FCSTD DOCUMENT  (FreeCAD 0.17R11939 (Git))
Label: front_head_tube_position
License: All rights reserved
LicenseURL: http://en.wikipedia.org/wiki/All_rights_reserved
objects: Sketcher::SketchObject×1
note: 1 computed .brp shape members not serialized (recipe doc carries the construction recipe); baked Part::Feature solids carry a one-line shape summary decoded from their .brp

FEATURE [Sketcher::SketchObject] Sketch
  expr: Constraints[10] = 180 - 74
  sketch-geometry (17):
    g0: LineSegment StartX=25.7714 StartY=69.3917 StartZ=0 EndX=56.0915 EndY=-36.3471 EndZ=0
    g1: LineSegment StartX=20.5248 StartY=-46.5457 StartZ=0 EndX=-9.79528 EndY=59.1931 EndZ=0
    g2: LineSegment [constr] StartX=6.63271 StartY=1.9019 StartZ=0 EndX=42.1994 EndY=12.1005 EndZ=0
    g3: GeomPoint X=24.416 Y=7.00119 Z=0
    g4: LineSegment [constr] StartX=6.63271 StartY=1.9019 StartZ=0 EndX=0 EndY=0 EndZ=0
    g5: ArcOfCircle CenterX=0 CenterY=0 CenterZ=0 NormalX=0 NormalY=0 NormalZ=1 Radius=25.4 StartAngle=1.57494 EndAngle=5.26675
    g6: ArcOfCircle CenterX=0 CenterY=0 CenterZ=0 NormalX=0 NormalY=0 NormalZ=1 Radius=23.749 StartAngle=1.55526 EndAngle=5.28643
    g7: LineSegment [constr] StartX=-25.4 StartY=0 StartZ=0 EndX=-23.749 EndY=0 EndZ=0
    g8: LineSegment StartX=-9.79528 StartY=59.1931 StartZ=0 EndX=-8.20824 EndY=59.6482 EndZ=0
    g9: LineSegment StartX=-8.20824 StartY=59.6482 StartZ=0 EndX=22.1119 EndY=-46.0906 EndZ=0
    g10: LineSegment StartX=22.1119 StartY=-46.0906 StartZ=0 EndX=20.5248 EndY=-46.5457 EndZ=0
    g11: LineSegment StartX=25.7714 StartY=69.3917 StartZ=0 EndX=24.1844 EndY=68.9366 EndZ=0
    g12: LineSegment StartX=24.1844 StartY=68.9366 StartZ=0 EndX=54.5045 EndY=-36.8022 EndZ=0
    g13: LineSegment StartX=54.5045 StartY=-36.8022 StartZ=0 EndX=56.0915 EndY=-36.3471 EndZ=0
    g14: LineSegment [constr] StartX=-8.20824 StartY=59.6482 StartZ=0 EndX=24.1844 EndY=68.9366 EndZ=0
    g15: LineSegment [constr] StartX=22.1119 StartY=-46.0906 StartZ=0 EndX=54.5045 EndY=-36.8022 EndZ=0
    g16: LineSegment [constr] StartX=7.00122 StartY=-24.416 StartZ=0 EndX=13.6339 EndY=-22.5141 EndZ=0
  constraints (52):
    c: Parallel(g1,g0)
    c: Distance(g1) = 110
    c: PointOnObject(g2,g1)
    c: PointOnObject(g2,g0)
    c: Perpendicular(g0,g2)
    c: PointOnObject(g3,g2)
    c: Symmetric(g2,g2,g3)
    c: Coincident(g4,g2)
    c: Coincident(g4,g-1)
    c: Parallel(g4,g2)
    c: Angle(g1) = 1.85005
    c: Coincident(g5,g-1)
    c: PointOnObject(g5,g1)
    c: PointOnObject(g5,g1)
    c: Radius(g5) = 25.4
    c: Coincident(g6,g-1)
    c: PointOnObject(g6,g1)
    c: PointOnObject(g6,g1)
    c: Distance(g-1,g3) = 25.4
    c: PointOnObject(g7,g5)
    c: PointOnObject(g7,g6)
    c: Horizontal(g7)
    c: PointOnObject(g7,g-1)
    c: Distance(g7) = 1.651
    c: Coincident(g8,g1)
    c: Coincident(g9,g8)
    c: Coincident(g10,g9)
    c: Coincident(g11,g0)
    c: Coincident(g12,g11)
    c: Coincident(g13,g12)
    c: Coincident(g13,g0)
    c: Perpendicular(g12,g13)
    c: Perpendicular(g1,g10)
    c: Perpendicular(g1,g8)
    c: Perpendicular(g12,g11)
    c: Coincident(g14,g8)
    c: Coincident(g14,g11)
    c: Coincident(g15,g9)
    c: Coincident(g15,g12)
    c: Parallel(g1,g9)
    c: Parallel(g12,g0)
    c: Parallel(g8,g14)
    c: Parallel(g10,g15)
    c: Equal(g8,g11)
    c: Distance(g8) = 1.651
    c: Distance(g1,g0) = 37
    c: PointOnObject(g16,g5)
    c: PointOnObject(g16,g1)
    c: Tangent(g16,g5)
    c: Perpendicular(g1,g16)
    c: Coincident(g1,g10)
    c: Distance(g1,g16) = 25
